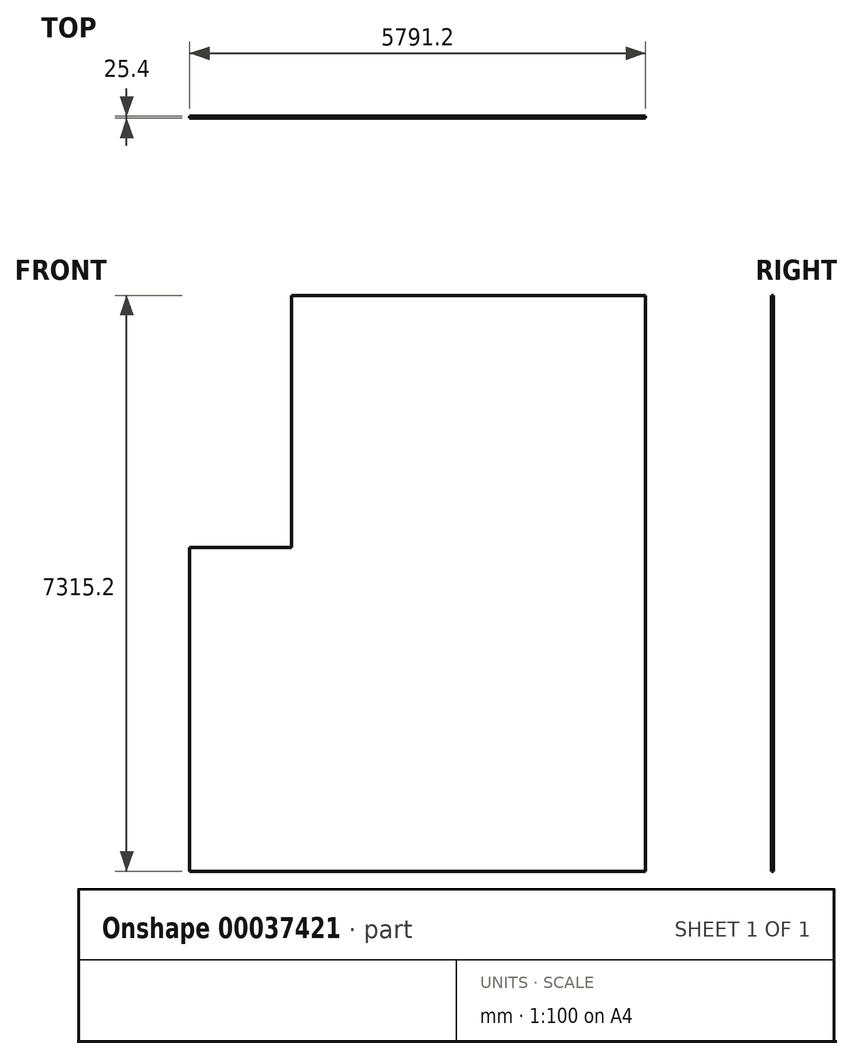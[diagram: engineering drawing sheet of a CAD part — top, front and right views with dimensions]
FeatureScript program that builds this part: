
annotation { "Feature Type Name" : "Feature", "Feature Type Description" : "" }
export const myFeature = defineFeature(function(context is Context, id is Id, definition is map)
    precondition{}
    {
        {
            var Q0;
            Q0=qCreatedBy(makeId("Front.planeOp"),FACE);
            var sketch = newSketch(context, id + "F0", { "sketchPlane" : qUnion([Q0])});
            skLineSegment(sketch, "E0", {"start": v(-5791.2, 0) * mm, "end": v(0, 0) * mm});
            skLineSegment(sketch, "E1", {"start": v(0, 0) * mm, "end": v(0, 7315.2) * mm});
            skLineSegment(sketch, "E2", {"start": v(0, 7315.2) * mm, "end": v(-4495.8, 7315.2) * mm});
            skLineSegment(sketch, "E3", {"start": v(-4495.8, 7315.2) * mm, "end": v(-4495.8, 4114.8) * mm});
            skLineSegment(sketch, "E4", {"start": v(-4495.8, 4114.8) * mm, "end": v(-5791.2, 4114.8) * mm});
            skLineSegment(sketch, "E5", {"start": v(-5791.2, 4114.8) * mm, "end": v(-5791.2, 0) * mm});
            skSolve(sketch);
        }
        {
            var Q0;
            Q0 = qSketchRegion(id + "F0", true);
            extrude(context, id + "F1", {"entities" : qUnion([Q0]), "depth" : 25.4 * mm});
        }
    });
